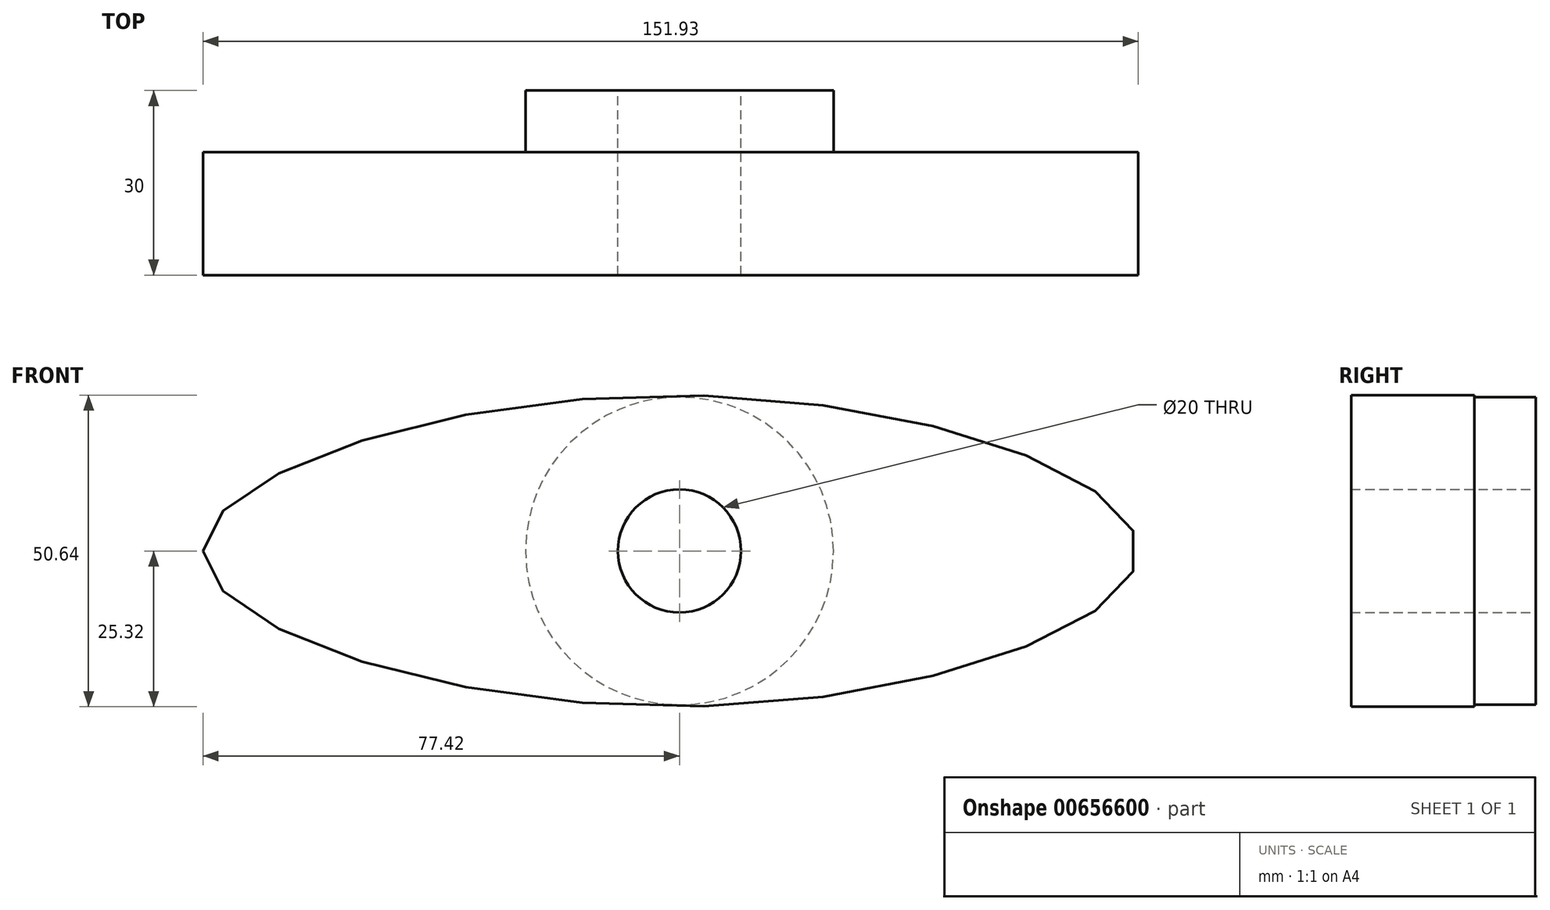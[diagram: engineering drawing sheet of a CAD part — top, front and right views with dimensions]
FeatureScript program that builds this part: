
annotation { "Feature Type Name" : "Feature", "Feature Type Description" : "" }
export const myFeature = defineFeature(function(context is Context, id is Id, definition is map)
    precondition{}
    {
        {
            var Q0;
            Q0=qCreatedBy(makeId("Front.planeOp"),FACE);
            var sketch = newSketch(context, id + "F0", { "sketchPlane" : qUnion([Q0])});
            skCircle(sketch, "E0", {"center": v(0, 0) * mm, "radius": 25 * mm});
            skSolve(sketch);
        }
        {
            var Q0;
            Q0 = qSketchRegion(id + "F0", true);
            extrude(context, id + "F1", {"entities" : qUnion([Q0]), "endBound" : BoundingType.SYMMETRIC, "depth" : 20 * mm, "offsetDistance" : 25.4 * mm});
        }
        {
            var Q0;
            Q0=qCreatedBy(makeId("Front.planeOp"),FACE);
            var sketch = newSketch(context, id + "F2", { "sketchPlane" : qUnion([Q0])});
            skCircle(sketch, "E1", {"center": v(0, 0) * mm, "radius": 15 * mm});
            skSolve(sketch);
        }
        {
            var Q0;
            Q0 = qSketchRegion(id + "F2", true);
            extrude(context, id + "F3", {"entities" : qUnion([Q0]), "operationType" : NewBodyOperationType.REMOVE, "endBound" : BoundingType.UP_TO_NEXT, "depth" : 20 * mm, "offsetDistance" : 25.4 * mm});
        }
        {
            var Q0;
            Q0=qCreatedBy(makeId("Front.planeOp"),FACE);
            var sketch = newSketch(context, id + "F4", { "sketchPlane" : qUnion([Q0])});
            skFitSpline(sketch, "E2", {"points": [v(-77.42, 0) * mm, v(0, 25.31) * mm, v(74.5, 0) * mm, v(0, -25.32) * mm, v(-77.42, 0) * mm]});
            skSolve(sketch);
        }
        {
            var Q0;
            Q0 = qSketchRegion(id + "F4", true);
            extrude(context, id + "F5", {"entities" : qUnion([Q0]), "operationType" : NewBodyOperationType.ADD, "depth" : 20 * mm, "offsetDistance" : 25.4 * mm});
        }
        {
            var Q0;
            Q0=makeQuery(id+"F5.opExtrude","CAP_FACE",FACE,{"disambiguationData":[OSD([sQuery(id+"F4.wireOp",EDGE,"E2")])],"isStart":true});
            var sketch = newSketch(context, id + "F6", { "sketchPlane" : qUnion([Q0])});
            skCircle(sketch, "E3", {"center": v(0, 0) * mm, "radius": 10 * mm});
            skSolve(sketch);
        }
        {
            var Q0;
            Q0 = qSketchRegion(id + "F6", true);
            extrude(context, id + "F7", {"entities" : qUnion([Q0]), "operationType" : NewBodyOperationType.REMOVE, "endBound" : BoundingType.SYMMETRIC, "oppositeDirection" : true, "depth" : 50 * mm, "offsetDistance" : 25.4 * mm});
        }
    });
